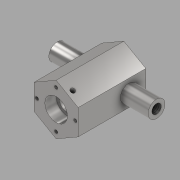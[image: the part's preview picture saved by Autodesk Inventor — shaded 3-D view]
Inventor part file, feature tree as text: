
AUTODESK INVENTOR PART (.ipt)
format: ipt  version: 2020 (Build 240168000, 168)  size: 174,080 bytes
history: native  units: in
note: dims shown in document units (in); Inventor stores cm internally (conversion verified against a paired STEP export)
features: sketch x7, hole x4, extrude x3, other x1, chamfer x1
ambient origin geometry x8: Origin, YZ Plane, XZ Plane, XY Plane, X Axis, Y Axis, Z Axis, Center Point
bodies: Body1 (feature_tree)
feature tree (16):
  other  "Sólido1"
  extrude  "Hexagono"  Depth=1.7in
  hole  "Tornillos"  [1 undecoded]
  extrude  "Extrusión2"  Depth=0.375in
  hole  "Agujero3"  [1 undecoded]
  chamfer  "Chaflán2"  Distance=1.125in
  extrude  "Extrusión3"  Depth=0.75in
  hole  "Agujero4"  [1 undecoded]
  hole  "Agujero5"  [1 undecoded]
  sketch  "Boceto1"  dims[d1=2.25in d2=1.7in]
  sketch  "Boceto2"  dims[d3=3.0in d4=0.0in d5=1.7in]
  sketch  "Boceto3"  dims[d6=0.145in d7=0.56in d8=0.375in d9=0.25in d10=0.5635in d11=0.56in d12=0.8108in d13=1.5in]
  sketch  "Boceto5"  dims[d14=1.5in d15=0.0in]
  sketch  "Boceto6"  dims[d26=0.75in d27=0.56in d28=1.0in d29=0.5in d30=0.5635in d31=0.63in d32=0.0in d33=0.375in d34=0.125in d35=45.0deg]
  sketch  "Boceto7"  dims[d36=0.75in]
  sketch  "Boceto8"  dims[d37=2.25in d38=1.125in d39=0.75in d40=4.4in d41=0.0in d42=0.417in d43=1.0in d44=0.5in d45=4.4in d46=0.5635in d47=1.385in d48=0.0in d49=0.25in d50=2.25in d51=1.125in d52=0.145in d53=0.38in d54=0.2in d55=0.375in d56=0.5635in d57=0.588in d58=0.0in]
note: 4 required parameter values undecoded (feature->parameter linkage not recoverable at this tier; creation-order binding heuristic only, values carry confidence <= 0.55)
